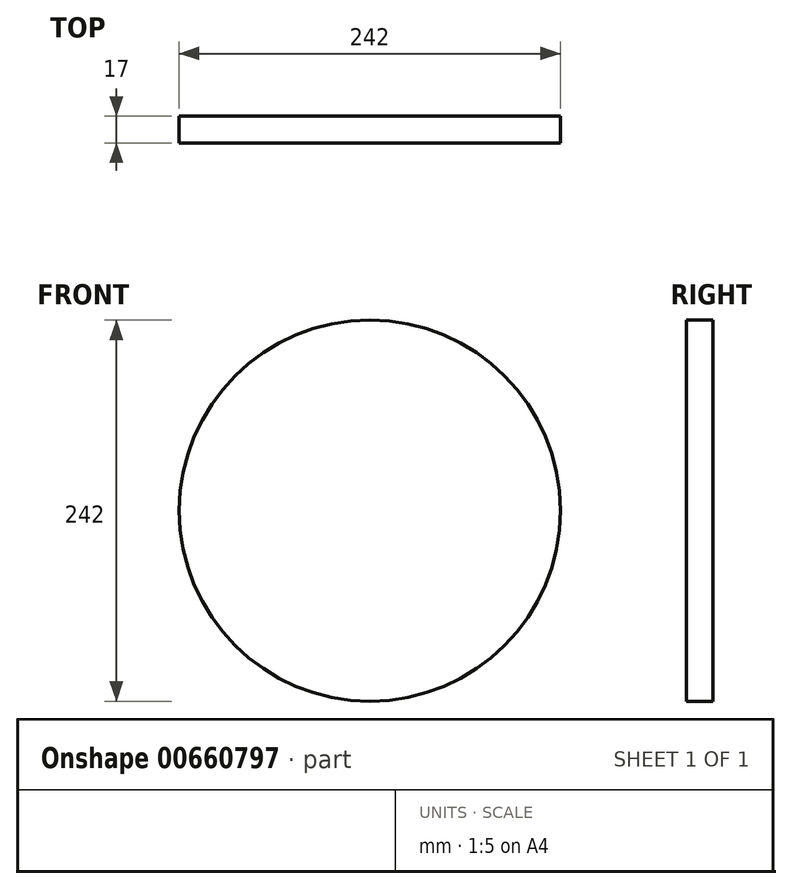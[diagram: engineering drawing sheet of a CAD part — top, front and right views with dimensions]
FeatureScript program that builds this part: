
annotation { "Feature Type Name" : "Feature", "Feature Type Description" : "" }
export const myFeature = defineFeature(function(context is Context, id is Id, definition is map)
    precondition{}
    {
        {
            var Q0;
            Q0=qCreatedBy(makeId("Front.planeOp"),FACE);
            var sketch = newSketch(context, id + "F0", { "sketchPlane" : qUnion([Q0])});
            skCircle(sketch, "E0", {"center": v(0, 0) * mm, "radius": 121 * mm});
            skSolve(sketch);
        }
        {
            var Q0;
            Q0=makeQuery(id+"F0.imprint","IMPRINT",FACE,{"disambiguationData":[TD([[makeQuery(id+"F0.imprint","IMPRINT",EDGE,{"derivedFrom":sQuery(id+"F0.wireOp",EDGE,"E0")}),1.0]])]});
            extrude(context, id + "F1", {"entities" : qUnion([Q0]), "depth" : 17 * mm, "offsetDistance" : 25.4 * mm});
        }
    });
